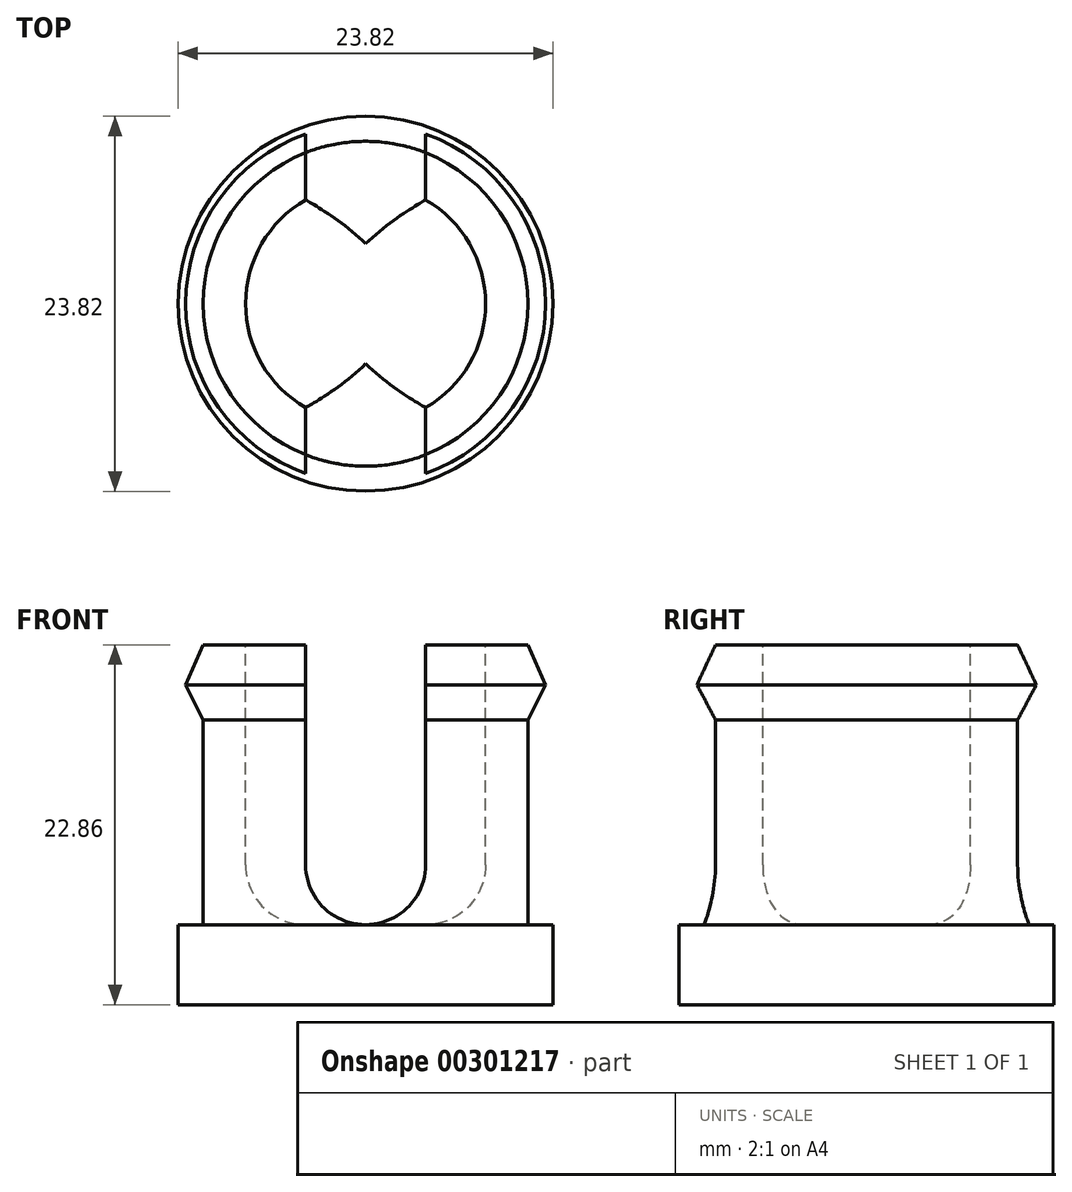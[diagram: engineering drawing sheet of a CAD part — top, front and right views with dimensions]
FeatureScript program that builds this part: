
annotation { "Feature Type Name" : "Feature", "Feature Type Description" : "" }
export const myFeature = defineFeature(function(context is Context, id is Id, definition is map)
    precondition{}
    {
        {
            var Q0;
            Q0=qCreatedBy(makeId("Front.planeOp"),FACE);
            var sketch = newSketch(context, id + "F0", { "sketchPlane" : qUnion([Q0])});
            skLineSegment(sketch, "E0", {"start": v(-11.9, 0) * mm, "end": v(-11.9, 5.08) * mm});
            skLineSegment(sketch, "E1", {"start": v(-11.9, 5.08) * mm, "end": v(-10.32, 5.08) * mm});
            skLineSegment(sketch, "E2", {"start": v(-10.32, 5.08) * mm, "end": v(-10.32, 18.08) * mm});
            skLineSegment(sketch, "E3", {"start": v(-10.32, 18.08) * mm, "end": v(-11.43, 20.32) * mm});
            skLineSegment(sketch, "E4", {"start": v(-11.43, 20.32) * mm, "end": v(-10.32, 22.86) * mm});
            skLineSegment(sketch, "E5", {"start": v(-10.32, 22.86) * mm, "end": v(0, 22.86) * mm});
            skLineSegment(sketch, "E6", {"start": v(-11.9, 0) * mm, "end": v(0, 0) * mm});
            skLineSegment(sketch, "E7", {"start": v(0, 22.86) * mm, "end": v(0, 0) * mm});
            skSolve(sketch);
        }
        {
            var Q0;
            Q0=qCreatedBy(makeId("Front.planeOp"),FACE);
            var sketch = newSketch(context, id + "F1", { "sketchPlane" : qUnion([Q0])});
            skLineSegment(sketch, "E8", {"start": v(0, -7.27) * mm, "end": v(0, 22.04) * mm});
            skSolve(sketch);
        }
        {
            var Q0;
            Q0 = qSketchRegion(id + "F0", true);
            var Q1;
            Q1=sQuery(id+"F1.wireOp",EDGE,"E8");
            revolve(context, id + "F2", {"entities" : qUnion([Q0]), "axis" : qUnion([Q1]), "revolveType" : RevolveType.FULL});
        }
        {
            var Q0;
            Q0=makeQuery(id+"F2.opRevolve","SWEPT_FACE",FACE,{"disambiguationData":[OSD([sQuery(id+"F0.wireOp",EDGE,"E5")])]});
            var sketch = newSketch(context, id + "F3", { "sketchPlane" : qUnion([Q0])});
            skCircle(sketch, "E9", {"center": v(0, 0) * mm, "radius": 7.62 * mm});
            skSolve(sketch);
        }
        {
            var Q0;
            Q0 = qSketchRegion(id + "F3", true);
            var Q1;
            Q1=makeQuery(id+"F2.opRevolve","SWEPT_FACE",FACE,{"disambiguationData":[OSD([sQuery(id+"F0.wireOp",EDGE,"E1")])]});
            extrude(context, id + "F4", {"entities" : qUnion([Q0]), "operationType" : NewBodyOperationType.REMOVE, "endBound" : BoundingType.UP_TO_SURFACE, "oppositeDirection" : true, "endBoundEntityFace" : qUnion([Q1]), "depth" : 25.4 * mm});
        }
        {
            var Q0;
            Q0=makeQuery(id+"F4.boolean.opBoolean","COPY",FACE,{"derivedFrom":makeQuery(id+"F4.opExtrude","CAP_FACE",FACE,{"disambiguationData":[OSD([sQuery(id+"F3.wireOp",EDGE,"E9")])],"isStart":false})});
            var sketch = newSketch(context, id + "F5", { "sketchPlane" : qUnion([Q0])});
            skLineSegment(sketch, "E10.0", {"start": v(-3.81, 14.03) * mm, "end": v(-3.81, 3.8) * mm});
            skLineSegment(sketch, "E11.0", {"start": v(3.81, 14.03) * mm, "end": v(3.81, 3.81) * mm});
            skLineSegment(sketch, "E12", {"start": v(-3.81, -15.09) * mm, "end": v(3.81, -15.09) * mm});
            skLineSegment(sketch, "E13", {"start": v(-3.81, 14.03) * mm, "end": v(3.81, 14.03) * mm});
            skLineSegment(sketch, "E14.trimOffspring", {"start": v(-3.81, 3.8) * mm, "end": v(-3.81, -15.09) * mm});
            skLineSegment(sketch, "E15.trimOffspring", {"start": v(3.81, 3.81) * mm, "end": v(3.81, -15.09) * mm});
            skSolve(sketch);
        }
        {
            var Q0;
            Q0 = qSketchRegion(id + "F5", true);
            extrude(context, id + "F6", {"entities" : qUnion([Q0]), "operationType" : NewBodyOperationType.REMOVE, "depth" : 25.4 * mm});
        }
        {
            var Q0;
            {var subQ0=sQuery(id+"F5.wireOp",EDGE,"E14.trimOffspring");var subQ1=sQuery(id+"F5.wireOp",EDGE,"E10.0");var subQ2=sQuery(id+"F3.wireOp",EDGE,"E9");Q0=makeQuery(id+"F6.boolean.opBoolean","SPLIT",EDGE,{"disambiguationData":[TD([makeQuery(id+"F6.opExtrude","SWEPT_FACE",FACE,{"disambiguationData":[OSD([subQ1,subQ0])]})])],"derivedFrom":makeQuery(id+"F4.boolean.opBoolean","COPY",EDGE,{"derivedFrom":makeQuery(id+"F4.opExtrude","CAP_EDGE",EDGE,{"disambiguationData":[OSD([subQ2])],"isStart":false})})});}
            var Q1;
            {var subQ0=sQuery(id+"F5.wireOp",EDGE,"E14.trimOffspring");var subQ1=sQuery(id+"F5.wireOp",EDGE,"E10.0");var subQ2=sQuery(id+"F3.wireOp",EDGE,"E9");Q1=makeQuery(id+"F6.boolean.opBoolean","SPLIT",EDGE,{"disambiguationData":[TD([makeQuery(id+"F6.opExtrude","SWEPT_FACE",FACE,{"disambiguationData":[OSD([subQ1,subQ0])]})])],"derivedFrom":makeQuery(id+"F4.boolean.opBoolean","COPY",EDGE,{"derivedFrom":makeQuery(id+"F4.opExtrude","CAP_EDGE",EDGE,{"disambiguationData":[OSD([subQ2])],"isStart":false})})});}
            var Q2;
            {var subQ0=sQuery(id+"F5.wireOp",EDGE,"c6699705-e2ac-4057-a69b-dff19f9b4a75.0");var subQ1=sQuery(id+"F3.wireOp",EDGE,"E9");var subQ2=sQuery(id+"F0.wireOp",EDGE,"E1");var subQ3=makeQuery(id+"F2.opRevolve","SWEPT_FACE",FACE,{"disambiguationData":[OSD([subQ2])]});Q2=makeQuery(id+"F6.boolean.opBoolean","SPLIT",EDGE,{"disambiguationData":[TD([makeQuery(id+"F6.opExtrude","SWEPT_FACE",FACE,{"disambiguationData":[OSD([subQ0])]})])],"derivedFrom":makeQuery(id+"F4.boolean.opBoolean","COPY",EDGE,{"derivedFrom":makeQuery(id+"F4.opExtrude","TWEAK_EDGE",EDGE,{"derivedFrom":[subQ3,makeQuery(id+"F3.imprint","IMPRINT",EDGE,{"derivedFrom":subQ1})]})})});}
            var Q3;
            {var subQ1=sQuery(id+"F5.wireOp",EDGE,"2a57cca4-0297-465d-8b72-82e5932dcbaf.0");var subQ2=sQuery(id+"F3.wireOp",EDGE,"E9");var subQ3=sQuery(id+"F0.wireOp",EDGE,"E1");var subQ4=makeQuery(id+"F2.opRevolve","SWEPT_FACE",FACE,{"disambiguationData":[OSD([subQ3])]});Q3=makeQuery(id+"F6.boolean.opBoolean","SPLIT",EDGE,{"disambiguationData":[TD([makeQuery(id+"F6.opExtrude","SWEPT_FACE",FACE,{"disambiguationData":[OSD([subQ1])]})])],"derivedFrom":makeQuery(id+"F4.boolean.opBoolean","COPY",EDGE,{"derivedFrom":makeQuery(id+"F4.opExtrude","TWEAK_EDGE",EDGE,{"derivedFrom":[subQ4,makeQuery(id+"F3.imprint","IMPRINT",EDGE,{"derivedFrom":subQ2})]})})});}
            var Q4;
            {var subQ0=sQuery(id+"F5.wireOp",EDGE,"E15.trimOffspring");var subQ1=sQuery(id+"F5.wireOp",EDGE,"E11.0");var subQ2=sQuery(id+"F3.wireOp",EDGE,"E9");Q4=makeQuery(id+"F6.boolean.opBoolean","SPLIT",EDGE,{"disambiguationData":[TD([makeQuery(id+"F6.opExtrude","SWEPT_FACE",FACE,{"disambiguationData":[OSD([subQ1,subQ0])]})])],"derivedFrom":makeQuery(id+"F4.boolean.opBoolean","COPY",EDGE,{"derivedFrom":makeQuery(id+"F4.opExtrude","CAP_EDGE",EDGE,{"disambiguationData":[OSD([subQ2])],"isStart":false})})});}
            var Q5;
            Q5=makeQuery(id+"F6.boolean.opBoolean","COPY",EDGE,{"disambiguationData":[OD(0.0)],"derivedFrom":makeQuery(id+"F6.opExtrude","CAP_EDGE",EDGE,{"disambiguationData":[OSD([sQuery(id+"F5.wireOp",EDGE,"E11.0"),sQuery(id+"F5.wireOp",EDGE,"E15.trimOffspring")])],"isStart":true})});
            var Q6;
            Q6=makeQuery(id+"F6.boolean.opBoolean","COPY",EDGE,{"disambiguationData":[OD(0.0)],"derivedFrom":makeQuery(id+"F6.opExtrude","CAP_EDGE",EDGE,{"disambiguationData":[OSD([sQuery(id+"F5.wireOp",EDGE,"E10.0"),sQuery(id+"F5.wireOp",EDGE,"E14.trimOffspring")])],"isStart":true})});
            var Q7;
            Q7=makeQuery(id+"F6.boolean.opBoolean","COPY",EDGE,{"disambiguationData":[OD(1.0)],"derivedFrom":makeQuery(id+"F6.opExtrude","CAP_EDGE",EDGE,{"disambiguationData":[OSD([sQuery(id+"F5.wireOp",EDGE,"E11.0"),sQuery(id+"F5.wireOp",EDGE,"E15.trimOffspring")])],"isStart":true})});
            var Q8;
            Q8=makeQuery(id+"F6.boolean.opBoolean","COPY",EDGE,{"disambiguationData":[OD(1.0)],"derivedFrom":makeQuery(id+"F6.opExtrude","CAP_EDGE",EDGE,{"disambiguationData":[OSD([sQuery(id+"F5.wireOp",EDGE,"E10.0"),sQuery(id+"F5.wireOp",EDGE,"E14.trimOffspring")])],"isStart":true})});
            fillet(context, id + "F7", {"entities" : qUnion([Q0, Q1, Q2, Q3, Q4, Q5, Q6, Q7, Q8]), "radius" : 3.8 * mm, "tangentPropagation" : true, "allowEdgeOverflow" : false});
        }
    });
